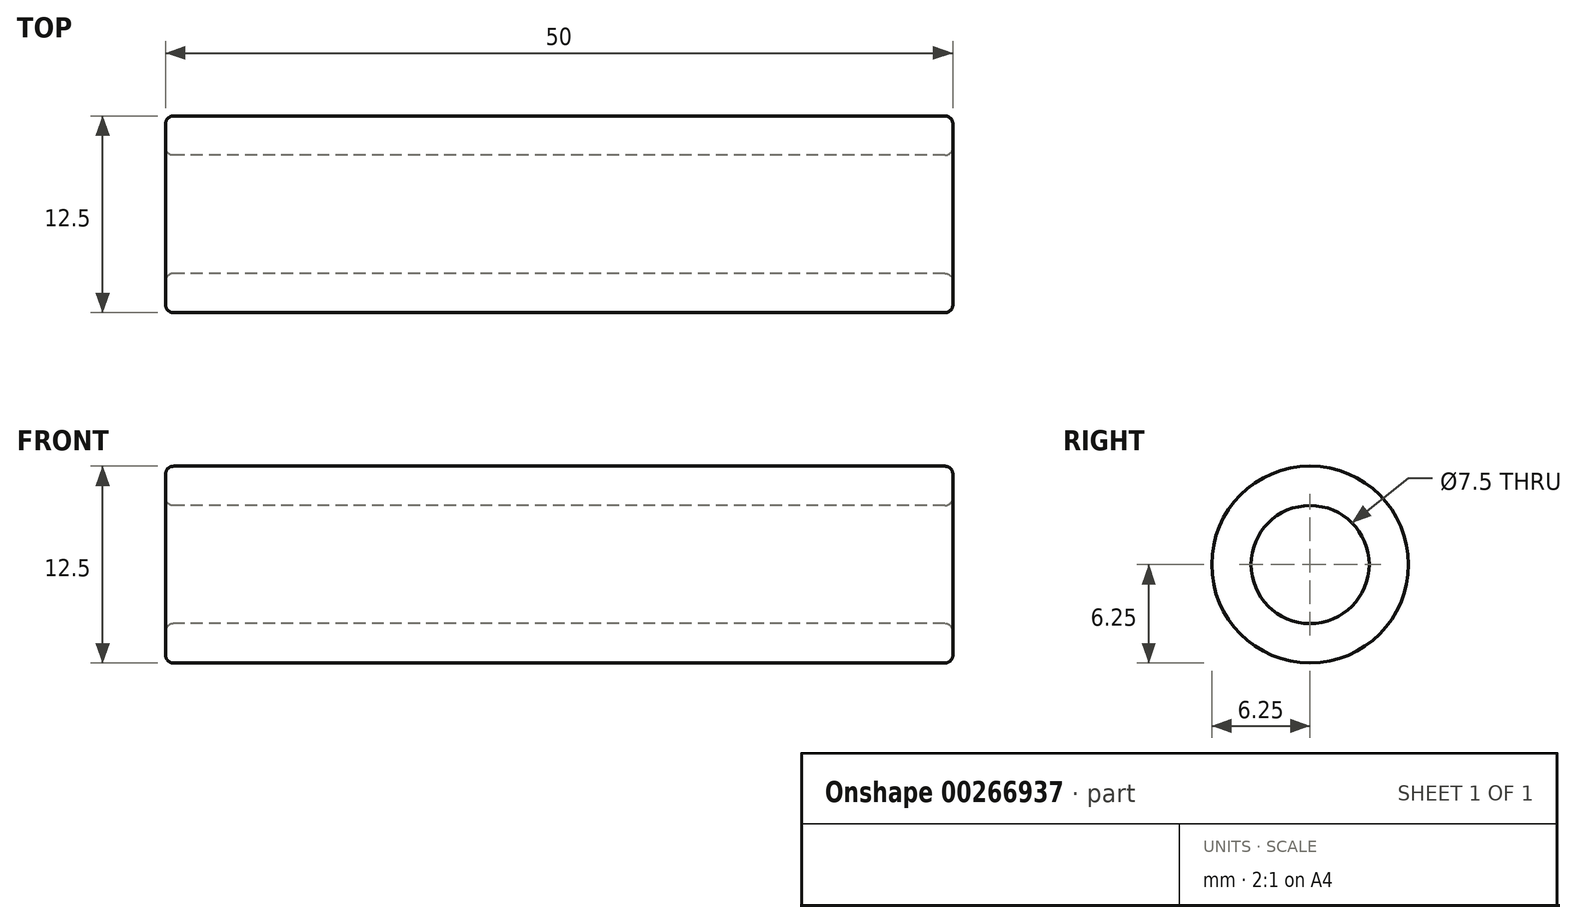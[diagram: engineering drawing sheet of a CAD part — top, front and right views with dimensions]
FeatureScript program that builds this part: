
annotation { "Feature Type Name" : "Feature", "Feature Type Description" : "" }
export const myFeature = defineFeature(function(context is Context, id is Id, definition is map)
    precondition{}
    {
        {
            var Q0;
            Q0=qCreatedBy(makeId("Right.planeOp"),FACE);
            var sketch = newSketch(context, id + "F0", { "sketchPlane" : qUnion([Q0])});
            skCircle(sketch, "E0", {"center": v(0, 0) * mm, "radius": 6.25 * mm});
            skCircle(sketch, "E1", {"center": v(0, 0) * mm, "radius": 3.75 * mm});
            skSolve(sketch);
        }
        {
            var Q0;
            Q0=makeQuery(id+"F0.imprint","IMPRINT",FACE,{"disambiguationData":[TD([[makeQuery(id+"F0.imprint","IMPRINT",EDGE,{"derivedFrom":sQuery(id+"F0.wireOp",EDGE,"E0")}),1.0]])]});
            extrude(context, id + "F1", {"entities" : qUnion([Q0]), "depth" : 50 * mm});
        }
        {
            var Q0;
            Q0=makeQuery(id+"F1.opExtrude","CAP_FACE",FACE,{"disambiguationData":[OSD([sQuery(id+"F0.wireOp",EDGE,"E0"),sQuery(id+"F0.wireOp",EDGE,"E1")])],"isStart":true});
            var Q1;
            Q1=makeQuery(id+"F1.opExtrude","CAP_FACE",FACE,{"disambiguationData":[OSD([sQuery(id+"F0.wireOp",EDGE,"E0"),sQuery(id+"F0.wireOp",EDGE,"E1")])],"isStart":false});
            fillet(context, id + "F2", {"entities" : qUnion([Q0, Q1]), "radius" : .5 * mm, "tangentPropagation" : true, "allowEdgeOverflow" : false});
        }
    });
